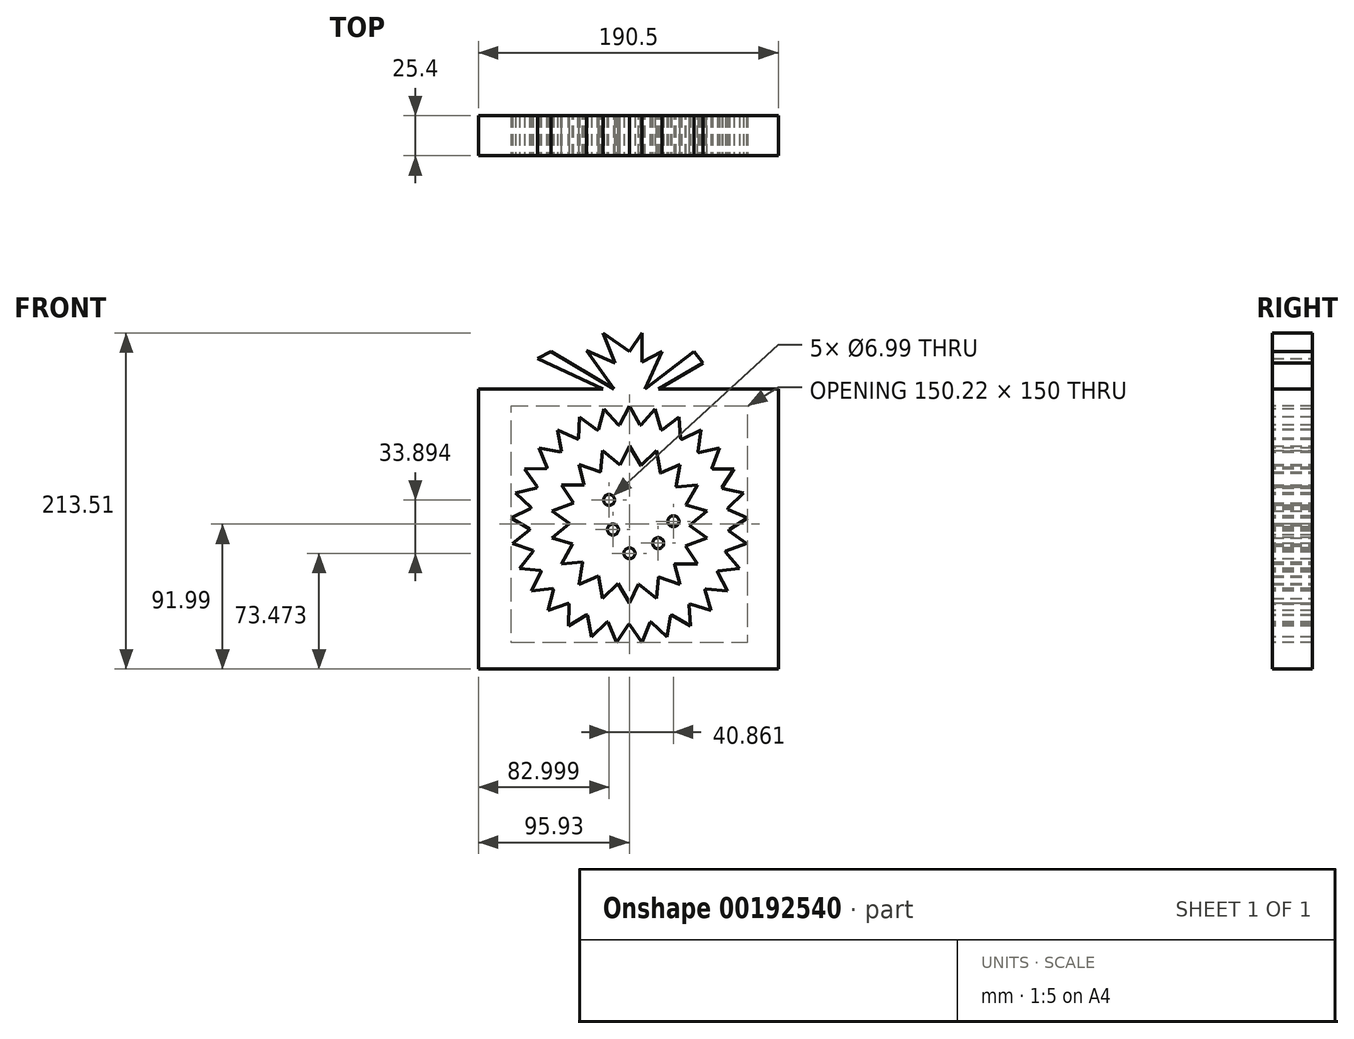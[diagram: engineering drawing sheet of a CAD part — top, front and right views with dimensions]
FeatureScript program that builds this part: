
annotation { "Feature Type Name" : "Feature", "Feature Type Description" : "" }
export const myFeature = defineFeature(function(context is Context, id is Id, definition is map)
    precondition{}
    {
        {
            var Q0;
            Q0=qCreatedBy(makeId("Front.planeOp"),FACE);
            var sketch = newSketch(context, id + "F0", { "sketchPlane" : qUnion([Q0])});
            skLineSegment(sketch, "E0", {"start": v(-6.7, 63.14) * mm, "end": v(0, 75.05) * mm});
            skLineSegment(sketch, "E1", {"start": v(0, 75.05) * mm, "end": v(6.09, 63.2) * mm});
            skLineSegment(sketch, "E2.1.0", {"start": v(-16.13, 73.3) * mm, "end": v(-7.64, 63.04) * mm});
            skLineSegment(sketch, "E2.1.1", {"start": v(-20.13, 60.23) * mm, "end": v(-16.13, 73.3) * mm});
            skLineSegment(sketch, "E2.2.0", {"start": v(-31.51, 68.12) * mm, "end": v(-21.02, 59.92) * mm});
            skLineSegment(sketch, "E2.2.1", {"start": v(-32.6, 54.5) * mm, "end": v(-31.51, 68.12) * mm});
            skLineSegment(sketch, "E2.3.0", {"start": v(-45.42, 59.75) * mm, "end": v(-33.4, 54) * mm});
            skLineSegment(sketch, "E2.3.1", {"start": v(-43.55, 46.2) * mm, "end": v(-45.42, 59.75) * mm});
            skLineSegment(sketch, "E2.4.0", {"start": v(-57.2, 48.59) * mm, "end": v(-44.23, 45.56) * mm});
            skLineSegment(sketch, "E2.4.1", {"start": v(-52.47, 35.77) * mm, "end": v(-57.2, 48.59) * mm});
            skLineSegment(sketch, "E2.5.0", {"start": v(-66.31, 35.16) * mm, "end": v(-53, 34.98) * mm});
            skLineSegment(sketch, "E2.5.1", {"start": v(-58.93, 23.65) * mm, "end": v(-66.31, 35.16) * mm});
            skLineSegment(sketch, "E2.6.0", {"start": v(-72.32, 20.08) * mm, "end": v(-59.28, 22.77) * mm});
            skLineSegment(sketch, "E2.6.1", {"start": v(-62.64, 10.43) * mm, "end": v(-72.32, 20.08) * mm});
            skLineSegment(sketch, "E2.7.0", {"start": v(-74.94, 4.06) * mm, "end": v(-62.79, 9.5) * mm});
            skLineSegment(sketch, "E2.7.1", {"start": v(-63.42, -3.28) * mm, "end": v(-74.94, 4.06) * mm});
            skLineSegment(sketch, "E2.8.0", {"start": v(-74.07, -12.14) * mm, "end": v(-63.36, -4.22) * mm});
            skLineSegment(sketch, "E2.8.1", {"start": v(-61.23, -16.84) * mm, "end": v(-74.07, -12.14) * mm});
            skLineSegment(sketch, "E2.9.0", {"start": v(-69.72, -27.78) * mm, "end": v(-60.97, -17.74) * mm});
            skLineSegment(sketch, "E2.9.1", {"start": v(-56.18, -29.6) * mm, "end": v(-69.72, -27.78) * mm});
            skLineSegment(sketch, "E2.10.0", {"start": v(-62.12, -42.12) * mm, "end": v(-55.73, -30.43) * mm});
            skLineSegment(sketch, "E2.10.1", {"start": v(-48.5, -40.99) * mm, "end": v(-62.12, -42.12) * mm});
            skLineSegment(sketch, "E2.11.0", {"start": v(-51.62, -54.49) * mm, "end": v(-47.89, -41.7) * mm});
            skLineSegment(sketch, "E2.11.1", {"start": v(-38.55, -50.46) * mm, "end": v(-51.62, -54.49) * mm});
            skLineSegment(sketch, "E2.12.0", {"start": v(-38.7, -64.31) * mm, "end": v(-37.8, -51.02) * mm});
            skLineSegment(sketch, "E2.12.1", {"start": v(-26.8, -57.56) * mm, "end": v(-38.7, -64.31) * mm});
            skLineSegment(sketch, "E2.13.0", {"start": v(-23.97, -71.13) * mm, "end": v(-25.95, -57.96) * mm});
            skLineSegment(sketch, "E2.13.1", {"start": v(-13.8, -61.98) * mm, "end": v(-23.97, -71.13) * mm});
            skLineSegment(sketch, "E2.14.0", {"start": v(-8.11, -74.61) * mm, "end": v(-12.88, -62.18) * mm});
            skLineSegment(sketch, "E2.14.1", {"start": v(-0.16, -63.5) * mm, "end": v(-8.11, -74.61) * mm});
            skLineSegment(sketch, "E2.15.0", {"start": v(8.11, -74.61) * mm, "end": v(0.78, -63.5) * mm});
            skLineSegment(sketch, "E2.15.1", {"start": v(13.5, -62.05) * mm, "end": v(8.11, -74.61) * mm});
            skLineSegment(sketch, "E2.16.0", {"start": v(23.97, -71.13) * mm, "end": v(14.41, -61.84) * mm});
            skLineSegment(sketch, "E2.16.1", {"start": v(26.52, -57.7) * mm, "end": v(23.97, -71.13) * mm});
            skLineSegment(sketch, "E2.17.0", {"start": v(38.7, -64.31) * mm, "end": v(27.37, -57.3) * mm});
            skLineSegment(sketch, "E2.17.1", {"start": v(38.3, -50.65) * mm, "end": v(38.7, -64.31) * mm});
            skLineSegment(sketch, "E2.18.0", {"start": v(51.62, -54.49) * mm, "end": v(39.05, -50.07) * mm});
            skLineSegment(sketch, "E2.18.1", {"start": v(48.3, -41.23) * mm, "end": v(51.62, -54.49) * mm});
            skLineSegment(sketch, "E2.19.0", {"start": v(62.12, -42.12) * mm, "end": v(48.9, -40.5) * mm});
            skLineSegment(sketch, "E2.19.1", {"start": v(56.03, -29.88) * mm, "end": v(62.12, -42.12) * mm});
            skLineSegment(sketch, "E2.20.0", {"start": v(69.72, -27.78) * mm, "end": v(56.47, -29.05) * mm});
            skLineSegment(sketch, "E2.20.1", {"start": v(61.14, -17.14) * mm, "end": v(69.72, -27.78) * mm});
            skLineSegment(sketch, "E2.21.0", {"start": v(74.07, -12.14) * mm, "end": v(61.4, -16.23) * mm});
            skLineSegment(sketch, "E2.21.1", {"start": v(63.4, -3.6) * mm, "end": v(74.07, -12.14) * mm});
            skLineSegment(sketch, "E2.22.0", {"start": v(74.94, 4.06) * mm, "end": v(63.44, -2.66) * mm});
            skLineSegment(sketch, "E2.22.1", {"start": v(62.69, 10.12) * mm, "end": v(74.94, 4.06) * mm});
            skLineSegment(sketch, "E2.23.0", {"start": v(72.32, 20.08) * mm, "end": v(62.53, 11.05) * mm});
            skLineSegment(sketch, "E2.23.1", {"start": v(59.05, 23.36) * mm, "end": v(72.32, 20.08) * mm});
            skLineSegment(sketch, "E2.24.0", {"start": v(66.31, 35.16) * mm, "end": v(58.7, 24.23) * mm});
            skLineSegment(sketch, "E2.24.1", {"start": v(52.65, 35.5) * mm, "end": v(66.31, 35.16) * mm});
            skLineSegment(sketch, "E2.25.0", {"start": v(57.2, 48.59) * mm, "end": v(52.11, 36.28) * mm});
            skLineSegment(sketch, "E2.25.1", {"start": v(43.78, 46) * mm, "end": v(57.2, 48.59) * mm});
            skLineSegment(sketch, "E2.26.0", {"start": v(45.42, 59.75) * mm, "end": v(43.1, 46.64) * mm});
            skLineSegment(sketch, "E2.26.1", {"start": v(32.87, 54.33) * mm, "end": v(45.42, 59.75) * mm});
            skLineSegment(sketch, "E2.27.0", {"start": v(31.51, 68.12) * mm, "end": v(32.06, 54.81) * mm});
            skLineSegment(sketch, "E2.27.1", {"start": v(20.43, 60.13) * mm, "end": v(31.51, 68.12) * mm});
            skLineSegment(sketch, "E2.28.0", {"start": v(16.13, 73.3) * mm, "end": v(19.53, 60.42) * mm});
            skLineSegment(sketch, "E2.28.1", {"start": v(7.02, 63.11) * mm, "end": v(16.13, 73.3) * mm});
            skPoint(sketch, "E2.center", {"position": v(0, 0) * mm});
            skLineSegment(sketch, "E3.bottom", {"start": v(-95.93, 86.03) * mm, "end": v(-16.72, 86.03) * mm});
            skLineSegment(sketch, "E3.top", {"start": v(-95.93, -91.77) * mm, "end": v(94.57, -91.77) * mm});
            skLineSegment(sketch, "E3.left", {"start": v(-95.93, 86.03) * mm, "end": v(-95.93, -91.77) * mm});
            skLineSegment(sketch, "E3.right", {"start": v(94.57, 86.03) * mm, "end": v(94.57, -91.77) * mm});
            skLineSegment(sketch, "E4", {"start": v(-16.72, 86.03) * mm, "end": v(-58.35, 105.4) * mm});
            skLineSegment(sketch, "E5", {"start": v(-58.35, 105.4) * mm, "end": v(-49.67, 110.02) * mm});
            skLineSegment(sketch, "E6", {"start": v(-49.67, 110.02) * mm, "end": v(-9.78, 86.03) * mm});
            skLineSegment(sketch, "E7", {"start": v(-9.78, 86.03) * mm, "end": v(-27.12, 110.6) * mm});
            skLineSegment(sketch, "E8", {"start": v(-27.12, 110.6) * mm, "end": v(-9.2, 102.5) * mm});
            skLineSegment(sketch, "E9", {"start": v(-9.2, 102.5) * mm, "end": v(-16.72, 121.58) * mm});
            skLineSegment(sketch, "E10", {"start": v(-16.72, 121.58) * mm, "end": v(0, 110.02) * mm});
            skLineSegment(sketch, "E11", {"start": v(0, 110.02) * mm, "end": v(8.1, 121.74) * mm});
            skLineSegment(sketch, "E12", {"start": v(8.1, 121.74) * mm, "end": v(8.1, 103.08) * mm});
            skLineSegment(sketch, "E13", {"start": v(8.1, 103.08) * mm, "end": v(20.87, 110.02) * mm});
            skLineSegment(sketch, "E14", {"start": v(20.87, 110.02) * mm, "end": v(9.88, 86.03) * mm});
            skLineSegment(sketch, "E15", {"start": v(9.88, 86.03) * mm, "end": v(41.1, 110.02) * mm});
            skLineSegment(sketch, "E16", {"start": v(41.1, 110.02) * mm, "end": v(46.75, 102.67) * mm});
            skLineSegment(sketch, "E17", {"start": v(46.75, 102.67) * mm, "end": v(18.55, 86.03) * mm});
            skLineSegment(sketch, "E18.trimOffspring", {"start": v(18.55, 86.03) * mm, "end": v(94.57, 86.03) * mm});
            skSolve(sketch);
        }
        {
            var Q0;
            Q0=qCreatedBy(makeId("Front.planeOp"),FACE);
            var sketch = newSketch(context, id + "F1", { "sketchPlane" : qUnion([Q0])});
            skLineSegment(sketch, "E19", {"start": v(-5.86, 37.69) * mm, "end": v(0, 49.9) * mm});
            skLineSegment(sketch, "E20", {"start": v(0, 49.9) * mm, "end": v(7.32, 37.43) * mm});
            skLineSegment(sketch, "E21.1.0", {"start": v(-17.07, 46.9) * mm, "end": v(-5.92, 37.67) * mm});
            skLineSegment(sketch, "E21.1.1", {"start": v(-18.4, 33.4) * mm, "end": v(-17.07, 46.9) * mm});
            skLineSegment(sketch, "E21.2.0", {"start": v(-32.08, 38.23) * mm, "end": v(-18.45, 33.38) * mm});
            skLineSegment(sketch, "E21.2.1", {"start": v(-28.71, 25.1) * mm, "end": v(-32.08, 38.23) * mm});
            skLineSegment(sketch, "E21.3.0", {"start": v(-43.22, 24.95) * mm, "end": v(-28.76, 25.05) * mm});
            skLineSegment(sketch, "E21.3.1", {"start": v(-35.57, 13.77) * mm, "end": v(-43.22, 24.95) * mm});
            skLineSegment(sketch, "E21.4.0", {"start": v(-49.15, 8.67) * mm, "end": v(-35.59, 13.7) * mm});
            skLineSegment(sketch, "E21.4.1", {"start": v(-38.13, 0.78) * mm, "end": v(-49.15, 8.67) * mm});
            skLineSegment(sketch, "E21.5.0", {"start": v(-49.15, -8.67) * mm, "end": v(-38.13, 0.7) * mm});
            skLineSegment(sketch, "E21.5.1", {"start": v(-36.1, -12.31) * mm, "end": v(-49.15, -8.67) * mm});
            skLineSegment(sketch, "E21.6.0", {"start": v(-43.22, -24.95) * mm, "end": v(-36.07, -12.38) * mm});
            skLineSegment(sketch, "E21.6.1", {"start": v(-29.7, -23.92) * mm, "end": v(-43.22, -24.95) * mm});
            skLineSegment(sketch, "E21.7.0", {"start": v(-32.08, -38.23) * mm, "end": v(-29.66, -23.97) * mm});
            skLineSegment(sketch, "E21.7.1", {"start": v(-19.74, -32.63) * mm, "end": v(-32.08, -38.23) * mm});
            skLineSegment(sketch, "E21.8.0", {"start": v(-17.07, -46.9) * mm, "end": v(-19.68, -32.67) * mm});
            skLineSegment(sketch, "E21.8.1", {"start": v(-7.38, -37.42) * mm, "end": v(-17.07, -46.9) * mm});
            skLineSegment(sketch, "E21.9.0", {"start": v(0, -49.9) * mm, "end": v(-7.32, -37.43) * mm});
            skLineSegment(sketch, "E21.9.1", {"start": v(5.86, -37.69) * mm, "end": v(0, -49.9) * mm});
            skLineSegment(sketch, "E21.10.0", {"start": v(17.07, -46.9) * mm, "end": v(5.92, -37.67) * mm});
            skLineSegment(sketch, "E21.10.1", {"start": v(18.4, -33.4) * mm, "end": v(17.07, -46.9) * mm});
            skLineSegment(sketch, "E21.11.0", {"start": v(32.08, -38.23) * mm, "end": v(18.45, -33.38) * mm});
            skLineSegment(sketch, "E21.11.1", {"start": v(28.71, -25.1) * mm, "end": v(32.08, -38.23) * mm});
            skLineSegment(sketch, "E21.12.0", {"start": v(43.22, -24.95) * mm, "end": v(28.76, -25.05) * mm});
            skLineSegment(sketch, "E21.12.1", {"start": v(35.57, -13.77) * mm, "end": v(43.22, -24.95) * mm});
            skLineSegment(sketch, "E21.13.0", {"start": v(49.15, -8.67) * mm, "end": v(35.59, -13.7) * mm});
            skLineSegment(sketch, "E21.13.1", {"start": v(38.13, -0.78) * mm, "end": v(49.15, -8.67) * mm});
            skLineSegment(sketch, "E21.14.0", {"start": v(49.15, 8.67) * mm, "end": v(38.13, -0.7) * mm});
            skLineSegment(sketch, "E21.14.1", {"start": v(36.1, 12.31) * mm, "end": v(49.15, 8.67) * mm});
            skLineSegment(sketch, "E21.15.0", {"start": v(43.22, 24.95) * mm, "end": v(36.07, 12.38) * mm});
            skLineSegment(sketch, "E21.15.1", {"start": v(29.7, 23.92) * mm, "end": v(43.22, 24.95) * mm});
            skLineSegment(sketch, "E21.16.0", {"start": v(32.08, 38.23) * mm, "end": v(29.66, 23.97) * mm});
            skLineSegment(sketch, "E21.16.1", {"start": v(19.74, 32.63) * mm, "end": v(32.08, 38.23) * mm});
            skLineSegment(sketch, "E21.17.0", {"start": v(17.07, 46.9) * mm, "end": v(19.68, 32.67) * mm});
            skLineSegment(sketch, "E21.17.1", {"start": v(7.38, 37.42) * mm, "end": v(17.07, 46.9) * mm});
            skCircle(sketch, "E22", {"center": v(0, 0) * mm, "radius": 38.14 * mm});
            skSolve(sketch);
        }
        {
            var Q0;
            Q0 = qSketchRegion(id + "F0", true);
            extrude(context, id + "F2", {"entities" : qUnion([Q0]), "depth" : 25.4 * mm});
        }
        {
            var Q0;
            Q0=makeQuery(id+"F2.opExtrude","CAP_FACE",FACE,{"disambiguationData":[OSD([sQuery(id+"F0.wireOp",EDGE,"E3.bottom"),sQuery(id+"F0.wireOp",EDGE,"E3.top"),sQuery(id+"F0.wireOp",EDGE,"E3.left"),sQuery(id+"F0.wireOp",EDGE,"E3.right"),sQuery(id+"F0.wireOp",EDGE,"E4"),sQuery(id+"F0.wireOp",EDGE,"E5"),sQuery(id+"F0.wireOp",EDGE,"E6"),sQuery(id+"F0.wireOp",EDGE,"E7"),sQuery(id+"F0.wireOp",EDGE,"E8"),sQuery(id+"F0.wireOp",EDGE,"E9"),sQuery(id+"F0.wireOp",EDGE,"E10"),sQuery(id+"F0.wireOp",EDGE,"E11"),sQuery(id+"F0.wireOp",EDGE,"E12"),sQuery(id+"F0.wireOp",EDGE,"E13"),sQuery(id+"F0.wireOp",EDGE,"E14"),sQuery(id+"F0.wireOp",EDGE,"E15"),sQuery(id+"F0.wireOp",EDGE,"E16"),sQuery(id+"F0.wireOp",EDGE,"E17"),sQuery(id+"F0.wireOp",EDGE,"E18.trimOffspring")])],"isStart":false});
            var sketch = newSketch(context, id + "F3", { "sketchPlane" : qUnion([Q0])});
            skCircle(sketch, "E23", {"center": v(0, 0) * mm, "radius": 63.5 * mm});
            skLineSegment(sketch, "E24", {"start": v(-6.28, 63.19) * mm, "end": v(0, 75.22) * mm});
            skLineSegment(sketch, "E25", {"start": v(0, 75.22) * mm, "end": v(6.7, 63.15) * mm});
            skLineSegment(sketch, "E26.1.0", {"start": v(-16.17, 73.46) * mm, "end": v(-7.04, 63.1) * mm});
            skLineSegment(sketch, "E26.1.1", {"start": v(-19.72, 60.36) * mm, "end": v(-16.17, 73.46) * mm});
            skLineSegment(sketch, "E26.2.0", {"start": v(-31.58, 68.27) * mm, "end": v(-20.44, 60.12) * mm});
            skLineSegment(sketch, "E26.2.1", {"start": v(-32.23, 54.71) * mm, "end": v(-31.58, 68.27) * mm});
            skLineSegment(sketch, "E26.3.0", {"start": v(-45.52, 59.88) * mm, "end": v(-32.89, 54.32) * mm});
            skLineSegment(sketch, "E26.3.1", {"start": v(-43.24, 46.5) * mm, "end": v(-45.52, 59.88) * mm});
            skLineSegment(sketch, "E26.4.0", {"start": v(-57.33, 48.7) * mm, "end": v(-43.8, 45.98) * mm});
            skLineSegment(sketch, "E26.4.1", {"start": v(-52.23, 36.12) * mm, "end": v(-57.33, 48.7) * mm});
            skLineSegment(sketch, "E26.5.0", {"start": v(-66.46, 35.23) * mm, "end": v(-52.66, 35.5) * mm});
            skLineSegment(sketch, "E26.5.1", {"start": v(-58.77, 24.05) * mm, "end": v(-66.46, 35.23) * mm});
            skLineSegment(sketch, "E26.6.0", {"start": v(-72.48, 20.12) * mm, "end": v(-59.05, 23.34) * mm});
            skLineSegment(sketch, "E26.6.1", {"start": v(-62.57, 10.85) * mm, "end": v(-72.48, 20.12) * mm});
            skLineSegment(sketch, "E26.7.0", {"start": v(-75.1, 4.07) * mm, "end": v(-62.7, 10.1) * mm});
            skLineSegment(sketch, "E26.7.1", {"start": v(-63.44, -2.85) * mm, "end": v(-75.1, 4.07) * mm});
            skLineSegment(sketch, "E26.8.0", {"start": v(-74.23, -12.17) * mm, "end": v(-63.4, -3.61) * mm});
            skLineSegment(sketch, "E26.8.1", {"start": v(-61.34, -16.42) * mm, "end": v(-74.23, -12.17) * mm});
            skLineSegment(sketch, "E26.9.0", {"start": v(-69.88, -27.84) * mm, "end": v(-61.14, -17.16) * mm});
            skLineSegment(sketch, "E26.9.1", {"start": v(-56.38, -29.23) * mm, "end": v(-69.88, -27.84) * mm});
            skLineSegment(sketch, "E26.10.0", {"start": v(-62.26, -42.21) * mm, "end": v(-56.02, -29.9) * mm});
            skLineSegment(sketch, "E26.10.1", {"start": v(-48.77, -40.66) * mm, "end": v(-62.26, -42.21) * mm});
            skLineSegment(sketch, "E26.11.0", {"start": v(-51.73, -54.6) * mm, "end": v(-48.28, -41.24) * mm});
            skLineSegment(sketch, "E26.11.1", {"start": v(-38.9, -50.2) * mm, "end": v(-51.73, -54.6) * mm});
            skLineSegment(sketch, "E26.12.0", {"start": v(-38.78, -64.45) * mm, "end": v(-38.29, -50.66) * mm});
            skLineSegment(sketch, "E26.12.1", {"start": v(-27.2, -57.38) * mm, "end": v(-38.78, -64.45) * mm});
            skLineSegment(sketch, "E26.13.0", {"start": v(-24.02, -71.28) * mm, "end": v(-26.5, -57.7) * mm});
            skLineSegment(sketch, "E26.13.1", {"start": v(-14.22, -61.89) * mm, "end": v(-24.02, -71.28) * mm});
            skLineSegment(sketch, "E26.14.0", {"start": v(-8.13, -74.78) * mm, "end": v(-13.48, -62.05) * mm});
            skLineSegment(sketch, "E26.14.1", {"start": v(-0.59, -63.5) * mm, "end": v(-8.13, -74.78) * mm});
            skLineSegment(sketch, "E26.15.0", {"start": v(8.13, -74.78) * mm, "end": v(0.17, -63.5) * mm});
            skLineSegment(sketch, "E26.15.1", {"start": v(13.08, -62.14) * mm, "end": v(8.13, -74.78) * mm});
            skLineSegment(sketch, "E26.16.0", {"start": v(24.02, -71.28) * mm, "end": v(13.82, -61.98) * mm});
            skLineSegment(sketch, "E26.16.1", {"start": v(26.13, -57.87) * mm, "end": v(24.02, -71.28) * mm});
            skLineSegment(sketch, "E26.17.0", {"start": v(38.78, -64.45) * mm, "end": v(26.82, -57.56) * mm});
            skLineSegment(sketch, "E26.17.1", {"start": v(37.96, -50.9) * mm, "end": v(38.78, -64.45) * mm});
            skLineSegment(sketch, "E26.18.0", {"start": v(51.73, -54.6) * mm, "end": v(38.57, -50.45) * mm});
            skLineSegment(sketch, "E26.18.1", {"start": v(48.02, -41.55) * mm, "end": v(51.73, -54.6) * mm});
            skLineSegment(sketch, "E26.19.0", {"start": v(62.26, -42.21) * mm, "end": v(48.5, -40.98) * mm});
            skLineSegment(sketch, "E26.19.1", {"start": v(55.83, -30.26) * mm, "end": v(62.26, -42.21) * mm});
            skLineSegment(sketch, "E26.20.0", {"start": v(69.88, -27.84) * mm, "end": v(56.18, -29.59) * mm});
            skLineSegment(sketch, "E26.20.1", {"start": v(61.03, -17.55) * mm, "end": v(69.88, -27.84) * mm});
            skLineSegment(sketch, "E26.21.0", {"start": v(74.23, -12.17) * mm, "end": v(61.23, -16.82) * mm});
            skLineSegment(sketch, "E26.21.1", {"start": v(63.37, -4.02) * mm, "end": v(74.23, -12.17) * mm});
            skLineSegment(sketch, "E26.22.0", {"start": v(75.1, 4.07) * mm, "end": v(63.42, -3.26) * mm});
            skLineSegment(sketch, "E26.22.1", {"start": v(62.76, 9.7) * mm, "end": v(75.1, 4.07) * mm});
            skLineSegment(sketch, "E26.23.0", {"start": v(72.48, 20.12) * mm, "end": v(62.64, 10.44) * mm});
            skLineSegment(sketch, "E26.23.1", {"start": v(59.2, 22.96) * mm, "end": v(72.48, 20.12) * mm});
            skLineSegment(sketch, "E26.24.0", {"start": v(66.46, 35.23) * mm, "end": v(58.93, 23.67) * mm});
            skLineSegment(sketch, "E26.24.1", {"start": v(52.88, 35.15) * mm, "end": v(66.46, 35.23) * mm});
            skLineSegment(sketch, "E26.25.0", {"start": v(57.33, 48.7) * mm, "end": v(52.46, 35.78) * mm});
            skLineSegment(sketch, "E26.25.1", {"start": v(44.1, 45.7) * mm, "end": v(57.33, 48.7) * mm});
            skLineSegment(sketch, "E26.26.0", {"start": v(45.52, 59.88) * mm, "end": v(43.54, 46.22) * mm});
            skLineSegment(sketch, "E26.26.1", {"start": v(33.24, 54.1) * mm, "end": v(45.52, 59.88) * mm});
            skLineSegment(sketch, "E26.27.0", {"start": v(31.58, 68.27) * mm, "end": v(32.59, 54.5) * mm});
            skLineSegment(sketch, "E26.27.1", {"start": v(20.83, 59.99) * mm, "end": v(31.58, 68.27) * mm});
            skLineSegment(sketch, "E26.28.0", {"start": v(16.17, 73.46) * mm, "end": v(20.11, 60.23) * mm});
            skLineSegment(sketch, "E26.28.1", {"start": v(7.45, 63.06) * mm, "end": v(16.17, 73.46) * mm});
            skSolve(sketch);
        }
        {
            var Q0;
            Q0 = qSketchRegion(id + "F3", true);
            extrude(context, id + "F4", {"entities" : qUnion([Q0]), "operationType" : NewBodyOperationType.REMOVE, "endBound" : BoundingType.THROUGH_ALL, "oppositeDirection" : true, "depth" : 25.4 * mm});
        }
        {
            var Q0;
            Q0 = qSketchRegion(id + "F1", true);
            extrude(context, id + "F5", {"entities" : qUnion([Q0]), "depth" : 25.4 * mm});
        }
        {
            var Q0;
            Q0=makeQuery(id+"F5.opExtrude","CAP_FACE",FACE,{"disambiguationData":[OSD([sQuery(id+"F1.wireOp",EDGE,"E19"),sQuery(id+"F1.wireOp",EDGE,"E20"),sQuery(id+"F1.wireOp",EDGE,"E21.1.0"),sQuery(id+"F1.wireOp",EDGE,"E21.1.1"),sQuery(id+"F1.wireOp",EDGE,"E21.2.0"),sQuery(id+"F1.wireOp",EDGE,"E21.2.1"),sQuery(id+"F1.wireOp",EDGE,"E21.3.0"),sQuery(id+"F1.wireOp",EDGE,"E21.3.1"),sQuery(id+"F1.wireOp",EDGE,"E21.4.0"),sQuery(id+"F1.wireOp",EDGE,"E21.4.1"),sQuery(id+"F1.wireOp",EDGE,"E21.5.0"),sQuery(id+"F1.wireOp",EDGE,"E21.5.1"),sQuery(id+"F1.wireOp",EDGE,"E21.6.0"),sQuery(id+"F1.wireOp",EDGE,"E21.6.1"),sQuery(id+"F1.wireOp",EDGE,"E21.7.0"),sQuery(id+"F1.wireOp",EDGE,"E21.7.1"),sQuery(id+"F1.wireOp",EDGE,"E21.8.0"),sQuery(id+"F1.wireOp",EDGE,"E21.8.1"),sQuery(id+"F1.wireOp",EDGE,"E21.9.0"),sQuery(id+"F1.wireOp",EDGE,"E21.9.1"),sQuery(id+"F1.wireOp",EDGE,"E21.10.0"),sQuery(id+"F1.wireOp",EDGE,"E21.10.1"),sQuery(id+"F1.wireOp",EDGE,"E21.11.0"),sQuery(id+"F1.wireOp",EDGE,"E21.11.1"),sQuery(id+"F1.wireOp",EDGE,"E21.12.0"),sQuery(id+"F1.wireOp",EDGE,"E21.12.1"),sQuery(id+"F1.wireOp",EDGE,"E21.13.0"),sQuery(id+"F1.wireOp",EDGE,"E21.13.1"),sQuery(id+"F1.wireOp",EDGE,"E21.14.0"),sQuery(id+"F1.wireOp",EDGE,"E21.14.1"),sQuery(id+"F1.wireOp",EDGE,"E21.15.0"),sQuery(id+"F1.wireOp",EDGE,"E21.15.1"),sQuery(id+"F1.wireOp",EDGE,"E21.16.0"),sQuery(id+"F1.wireOp",EDGE,"E21.16.1"),sQuery(id+"F1.wireOp",EDGE,"E21.17.0"),sQuery(id+"F1.wireOp",EDGE,"E21.17.1"),sQuery(id+"F1.wireOp",EDGE,"E22")])],"isStart":false});
            var sketch = newSketch(context, id + "F6", { "sketchPlane" : qUnion([Q0])});
            skCircle(sketch, "E27", {"center": v(-12.93, 15.6) * mm, "radius": 3.5 * mm});
            skCircle(sketch, "E28", {"center": v(-10.48, -3.19) * mm, "radius": 3.5 * mm});
            skCircle(sketch, "E29", {"center": v(0, -18.3) * mm, "radius": 3.5 * mm});
            skCircle(sketch, "E30", {"center": v(18.29, -11.86) * mm, "radius": 3.5 * mm});
            skCircle(sketch, "E31", {"center": v(27.93, 2.04) * mm, "radius": 3.5 * mm});
            skSolve(sketch);
        }
        {
            var Q0;
            Q0=makeQuery(id+"F6.imprint","IMPRINT",FACE,{"disambiguationData":[TD([[makeQuery(id+"F6.imprint","IMPRINT",EDGE,{"derivedFrom":sQuery(id+"F6.wireOp",EDGE,"E27")}),1.0]])]});
            var Q1;
            Q1=makeQuery(id+"F6.imprint","IMPRINT",FACE,{"disambiguationData":[TD([[makeQuery(id+"F6.imprint","IMPRINT",EDGE,{"derivedFrom":sQuery(id+"F6.wireOp",EDGE,"E28")}),1.0]])]});
            var Q2;
            Q2=makeQuery(id+"F6.imprint","IMPRINT",FACE,{"disambiguationData":[TD([[makeQuery(id+"F6.imprint","IMPRINT",EDGE,{"derivedFrom":sQuery(id+"F6.wireOp",EDGE,"E29")}),1.0]])]});
            var Q3;
            Q3=makeQuery(id+"F6.imprint","IMPRINT",FACE,{"disambiguationData":[TD([[makeQuery(id+"F6.imprint","IMPRINT",EDGE,{"derivedFrom":sQuery(id+"F6.wireOp",EDGE,"E30")}),1.0]])]});
            var Q4;
            Q4=makeQuery(id+"F6.imprint","IMPRINT",FACE,{"disambiguationData":[TD([[makeQuery(id+"F6.imprint","IMPRINT",EDGE,{"derivedFrom":sQuery(id+"F6.wireOp",EDGE,"E31")}),1.0]])]});
            extrude(context, id + "F7", {"entities" : qUnion([Q0, Q1, Q2, Q3, Q4]), "operationType" : NewBodyOperationType.REMOVE, "endBound" : BoundingType.THROUGH_ALL, "oppositeDirection" : true, "depth" : 25.4 * mm});
        }
    });
